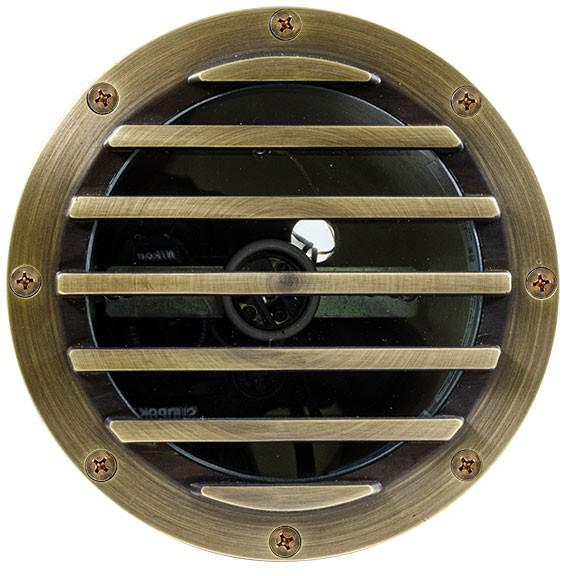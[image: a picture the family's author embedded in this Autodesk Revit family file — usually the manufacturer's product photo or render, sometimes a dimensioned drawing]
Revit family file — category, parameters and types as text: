
# Revit family: Alcon-9033-Revit-Family
name_source: partatom
category: Luminarias
units: mm (PartAtom-declared; Revit-internal decimal feet)

## family parameters
Anfitrión = Cara
Compartido = No
Corte con vacíos al cargar = No
Cota de conector redondo = Usar diámetro
Mantener orientación de anotación = No
Origen de luz = Sí
Punto de cálculo de habitación = No
Tipo de pieza = Normal

## types (1)
- Alcon-9033-Revit-Family
    Cambio de temperatura de color de luz atenuada = <Ninguno>
    Elevación por defecto = 4' - 0"
    Fabricante = Alcon Lighting
    Filtro de color = 16777215
    GLASS LENS = Analytical Panels
    HOUSING = <Por categoría>
    LENS GLASS = Glass
    Link to IES File = https://www.alconlighting.com
    Longitud de símbolo de origen de luz = 10' - 0"
    Modelo = Alcon Lighting 9033
    Product Data URL = https://www.alconlighting.com
    Product Page = https://www.alconlighting.com
    TAP LENS = <Por categoría>
    TOP FINISH = <Por categoría>
    URL = https://www.alconlighting.com
    Ángulo de campo de foco = 90.00°
    Ángulo de enfoque = 30.00°
    Ángulo de inclinación = 60.00°

## geometry (parser evidence)
native form markers: Sweep x3
no freeform markers — native parametric forms only
